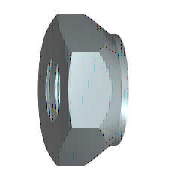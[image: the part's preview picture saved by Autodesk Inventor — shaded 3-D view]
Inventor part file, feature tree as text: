
AUTODESK INVENTOR PART (.ipt)
format: ipt  version: 2013 (Build 170138000, 138)  size: 181,760 bytes
history: native  units: mm (DEFAULTED — no unit token found)
features: sketch x3, hole x1, chamfer x1, other x1, plane x1
ambient origin geometry x7: Origin, YZ Plane, XZ Plane, X Axis, Y Axis, Z Axis, Center Point
bodies: Solid1 (feature_tree), Body (feature_tree)
feature tree (7):
  hole  "Thread"  [1 undecoded]
  chamfer  "Chamfer3"  Distance=8.0mm
  other  "Work Axis1"
  plane  "Work Plane1"
  sketch  "Sketch1"  dims[d0=9.237604mm d1=7.2mm]
  sketch  "Sketch3"  dims[d3=30.0deg d5=8.0mm d6=6.8mm d7=90.0deg d8=60.0deg d9=2.7mm d24=4.134mm d25=6.0mm d26=4.0mm d27=2.0mm d28=14.3117mm d29=8.0mm d30=20.594885mm d10=0.433013mm d11=30.0deg d12=0.433013mm d13=30.0deg d14=0.0mm d38=0.0mm d39=0.433013mm d40=0.433013mm d41=0.0mm d42=0.0mm]
  sketch  "Sketch2"  dims[d2=0.0mm]
note: 1 required parameter value undecoded (feature->parameter linkage not recoverable at this tier; creation-order binding heuristic only, values carry confidence <= 0.55)
